# Revit family: 2060655(n) 300
name_source: partatom
category: Security Devices
units: mm (PartAtom-declared; Revit-internal decimal feet)

## family parameters
Always vertical = No
Cut with Voids When Loaded = No
Host = Wall
OmniClass Number = 23.85.30.14
OmniClass Title = Presence Detection/Registration
Room Calculation Point = No
Shared = Yes

## types (2) — shared parameters
zero-valued in all types: A

## per-type parameters (varying)
- Type 1: CTN=0; EF000008=0 mm  [stored 0 ft]; EF000040=0 mm  [stored 0 ft]; EF000049=0 mm  [stored 0 ft]; EF000193=0; EF000194=0; EF000218=0 mm  [stored 0 ft]; EF000551=0 mm  [stored 0 ft]; EF000846=0 mm  [stored 0 ft]; EF001322=0 mm  [stored 0 ft]; EF001323=0 mm  [stored 0 ft]; EF003843=0 mm  [stored 0 ft]; EF003882=0; EF004101=0.00°; EF006589=0; EF006590=0; EF008011=0 mm  [stored 0 ft]; EF010517=0 mm  [stored 0 ft]; EF010886=0 mm  [stored 0 ft]; EF011019=0 mm  [stored 0 ft]; EF011020=0 mm  [stored 0 ft]; EF012278=0 mm  [stored 0 ft]; LOG=0; NOCUPEROU=0; PRICEQUANTITY=0; QUANTITYINT=0; QUANTITYMIN=0
- 2060655: ARTICLENO=NB; BOMINFO=LINA; CATALOG=Theben; COO=CN; CTN=90314990; DEEPLINK_PRODUKTSEITE=http://www.theben.de; DESCLONG=Passive infrared presence detector for flush wall mounting, 1 channel light and 1 channel presence, with Theben cover frame, semi-circular detection area 170° up to 14x17 m, automatic presence and brightness-dependent control for lighting, acoustic function and orientation light, automatic adjustment of brightness measurement, adjustable sensitivity, external pushbutton can be connected, Short-time presence, remote-controllable, operation as fully or semi-automatic, switchable, brightness switching value adjustable, teach-in function, staircase lighting and pulse function, switch-on delay and follow-up time adjustable, restriction of detection area possible, integrated pushbutton (can be blocked), extension of detection area via master/slave switching; DESCSHORT=Presence detector wall mounting, light and presence, with frame; EF000003=EV000383; EF000007=White; EF000008=85 mm  [stored 0.278871 ft]; EF000010=Presence detector; EF000025=false; EF000040=85 mm  [stored 0.278871 ft]; EF000049=57 mm  [stored 0.187008 ft]; EF000124=Plug-in clamp; EF000139=Untreated; EF000147=false; EF000187=AC; EF000193=3600; EF000194=1800; EF000218=40 mm  [stored 0.131234 ft]; EF000416=50, 60 Hz; EF000483=false; EF000551=54 mm  [stored 0.177165 ft]; EF000846=85 mm  [stored 0.278871 ft]; EF001098=true; EF001099=false; EF001198=false; EF001257=Thermoplast; EF001322=17000 mm  [stored 55.7743 ft]; EF001323=7000 mm; EF001731=-15, 45 °C; EF002169=Plastic; EF003429=true; EF003808=false; EF003814=5, 3000 lx; EF003832=false; EF003843=17000 mm  [stored 55.7743 ft]; EF003848=true; EF003858=true; EF003863=false; EF003876=true; EF003882=9010; EF003890=false; EF003898=true; EF003904=true; EF003920=false; EF004101=170.00°; EF004293=IK04; EF005474=IP20; EF005624=false; EF006243=false; EF006311=false; EF006569=shiny; EF006582=0, 170 °; EF006589=1; EF006590=60; EF006644=true; EF007575=true; EF008011=1200 mm; EF009569=false; EF010517=20 mm  [stored 0.0656168 ft]; EF010886=10 mm  [stored 0.0328084 ft]; EF011019=45 mm  [stored 0.147638 ft]; EF011020=50 mm  [stored 0.164042 ft]; EF011072=false; EF011991=false; EF012278=40 mm  [stored 0.131234 ft]; EF014925=false; EF014926=false; EF014927=false; EF020270=Passive infrared; EF021180=false; EF023790=false; GEBRAUCHSANLEITUNG=http://www.theben.de; INTNO=4003468200124; LINA=2060655; LOG=300; MANUID=2060655; MANUNAME=Theben AG; MANUTYPEDESC=theMura S180-101 UP WH; Manufacturer=Theben; Model=2060655; NB=2060655(N) 300; NBSYN=$MANUID.($SA.) $LOG.; NN=Presence detector 230 V; NOCUPEROU=1; PRICEQUANTITY=1; PRODUKTDATENBLATT=http://www.theben.de; QUANTITYINT=1; QUANTITYMIN=1; REACH_ERKLAERUNG=http://www.theben.de; REMARKS=ERP-GROUP 450; SA=None; SUPPLIER=THEBEN; SUPPLIERALTNO=2060655

note: [stored X ft] marks values corroborated as IEEE doubles in the binary element streams (Revit-internal decimal feet)

## geometry (parser evidence)
native form markers: Sweep x10
no freeform markers — native parametric forms only
